# Revit family: ToiletPaperDispenser_Metlam_Single_SurfaceMounted
name_source: partatom
category: Generic Models
revit_build: Autodesk Revit Architecture 2013 (Build: 20120221_2030(x64)
units: mm (PartAtom-declared; Revit-internal decimal feet)

## types (4) — shared parameters
Assembly Code = E1090900
Default Elevation = 1219 mm
Depth = 75 mm
Description = Stainless Steel Toilet Paper Dispenser
FilterObject_ANZRS = Toilet Paper Dispenser
Height = 161 mm  [stored 0.528215 ft]
Keywords = CAPACITY Dispenses one 1500 sheet roll
Manufacturer = Metlam
Material Minor = PC/ABS Plastic
ModifiedIssue_ANZRS = 130318.01 $
StyleOrType_ANZRS = Sanitary Ware
URL = http://www.metlam.com.au
Width = 161 mm  [stored 0.528215 ft]

## per-type parameters (varying)
| type | Hood | Material Main | Model | Product Code |
| Metlam Single Surface Mounted - no Hood / Satin | No | Stainless Steel, Satin | Single Surface Mounted - no Hood / Satin | ML 260 SM |
| Metlam Single Surface Mounted - no Hood / Bright | No | Stainless Steel, Polished | Single Surface Mounted - no Hood / Bright | ML 260 SMB |
| Metlam Single Surface Mounted - Hood / Satin | Yes | Stainless Steel, Satin | Single Surface Mounted - Hood / Satin | ML 261 SMS |
| Metlam Single Surface Mounted - Hood / Bright | Yes | Stainless Steel, Polished | Single Surface Mounted - Hood / Bright | ML 261 SMB |

note: [stored X ft] marks values corroborated as IEEE doubles in the binary element streams (Revit-internal decimal feet)

## geometry (parser evidence)
native form markers: Blend x12, Sweep x1
no freeform markers — native parametric forms only
